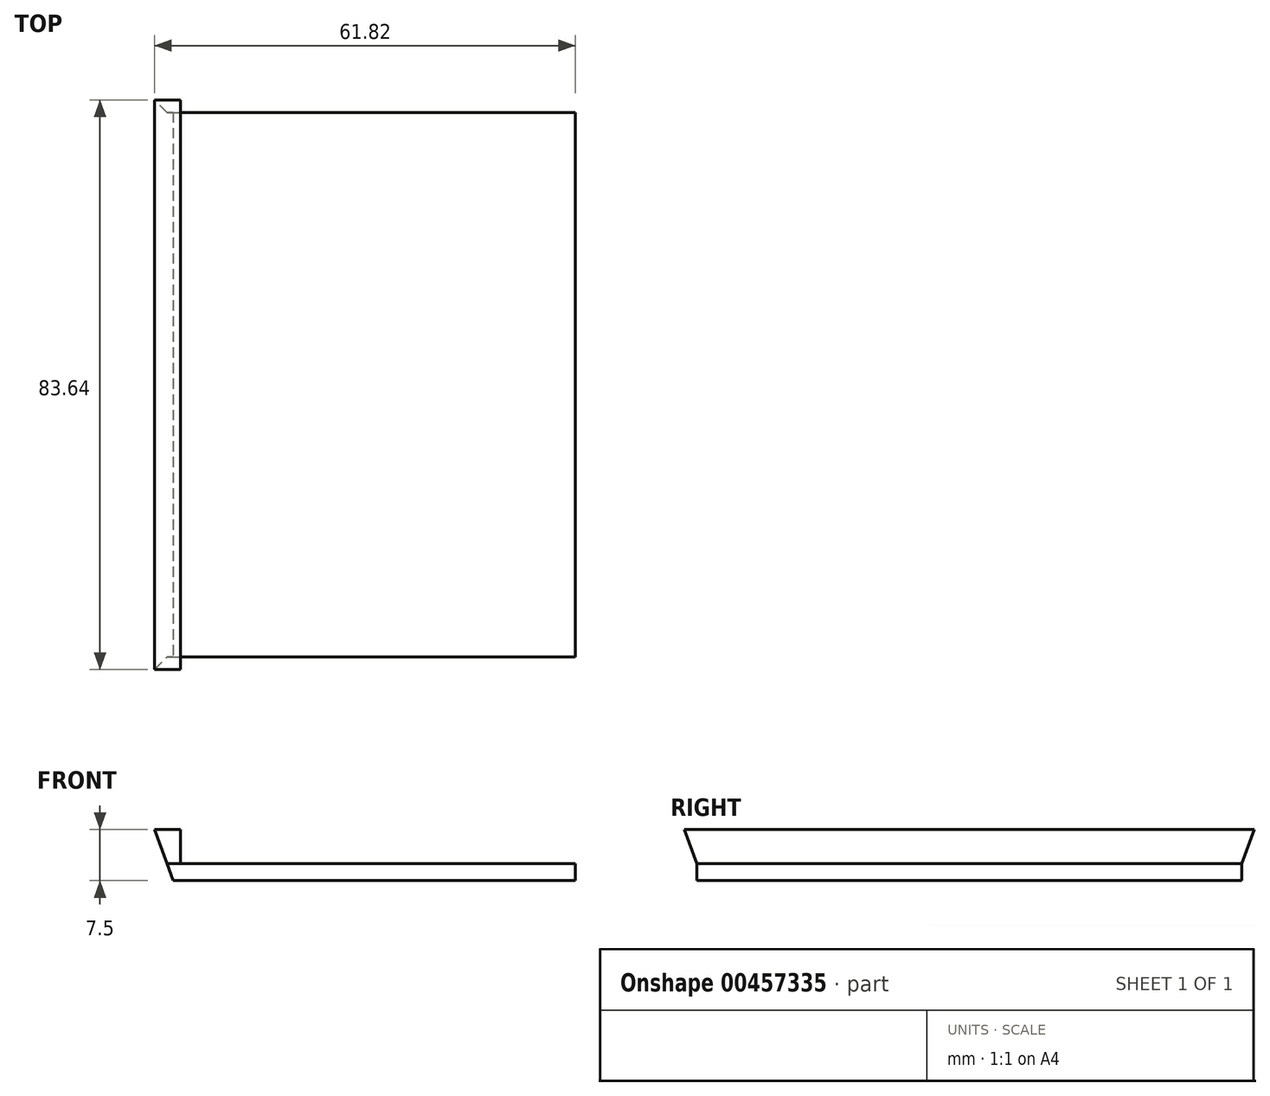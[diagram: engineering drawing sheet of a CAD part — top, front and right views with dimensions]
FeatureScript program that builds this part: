
annotation { "Feature Type Name" : "Feature", "Feature Type Description" : "" }
export const myFeature = defineFeature(function(context is Context, id is Id, definition is map)
    precondition{}
    {
        {
            var Q0;
            Q0=qCreatedBy(makeId("Top.planeOp"),FACE);
            var sketch = newSketch(context, id + "F0", { "sketchPlane" : qUnion([Q0])});
            skLineSegment(sketch, "E0.bottom", {"start": v(-22.39, 40.24) * mm, "end": v(37.61, 40.24) * mm});
            skLineSegment(sketch, "E0.top", {"start": v(-22.39, -39.76) * mm, "end": v(37.61, -39.76) * mm});
            skLineSegment(sketch, "E0.left", {"start": v(-22.39, 40.24) * mm, "end": v(-22.39, -39.76) * mm});
            skLineSegment(sketch, "E0.right", {"start": v(37.61, 40.24) * mm, "end": v(37.61, -39.76) * mm});
            skSolve(sketch);
        }
        {
            var Q0;
            Q0=makeQuery(id+"F0.imprint","IMPRINT",FACE,{"disambiguationData":[TD([[makeQuery(id+"F0.imprint","IMPRINT",EDGE,{"derivedFrom":sQuery(id+"F0.wireOp",EDGE,"E0.bottom")}),-1.0]])]});
            extrude(context, id + "F1", {"entities" : qUnion([Q0]), "depth" : 2.5 * mm});
        }
        {
            var Q0;
            Q0=makeQuery(id+"F1.opExtrude","CAP_FACE",FACE,{"disambiguationData":[OSD([sQuery(id+"F0.wireOp",EDGE,"E0.bottom"),sQuery(id+"F0.wireOp",EDGE,"E0.top"),sQuery(id+"F0.wireOp",EDGE,"E0.left"),sQuery(id+"F0.wireOp",EDGE,"E0.right")])],"isStart":false});
            var sketch = newSketch(context, id + "F2", { "sketchPlane" : qUnion([Q0])});
            skLineSegment(sketch, "E1.bottom", {"start": v(-22.39, 40.24) * mm, "end": v(-18.39, 40.24) * mm});
            skLineSegment(sketch, "E1.top", {"start": v(-22.39, -39.76) * mm, "end": v(-18.39, -39.76) * mm});
            skLineSegment(sketch, "E1.left", {"start": v(-22.39, 40.24) * mm, "end": v(-22.39, -39.76) * mm});
            skLineSegment(sketch, "E1.right", {"start": v(-18.39, 40.24) * mm, "end": v(-18.39, -39.76) * mm});
            skSolve(sketch);
        }
        {
            var Q0;
            Q0 = qSketchRegion(id + "F2", true);
            extrude(context, id + "F3", {"entities" : qUnion([Q0]), "operationType" : NewBodyOperationType.ADD, "depth" : 5 * mm, "hasDraft" : true, "draftAngle" : 20 * degree});
        }
        {
            var Q0;
            Q0=makeQuery(id+"F3.opExtrude","CAP_FACE",FACE,{"disambiguationData":[OSD([sQuery(id+"F2.wireOp",EDGE,"E1.bottom"),sQuery(id+"F2.wireOp",EDGE,"E1.top"),sQuery(id+"F2.wireOp",EDGE,"E1.left"),sQuery(id+"F2.wireOp",EDGE,"E1.right")])],"isStart":false});
            var sketch = newSketch(context, id + "F4", { "sketchPlane" : qUnion([Q0])});
            skLineSegment(sketch, "E2.bottom", {"start": v(-16.57, 42.06) * mm, "end": v(-20.39, 42.06) * mm});
            skLineSegment(sketch, "E2.top", {"start": v(-16.57, -41.58) * mm, "end": v(-20.39, -41.58) * mm});
            skLineSegment(sketch, "E2.left", {"start": v(-16.57, 42.06) * mm, "end": v(-16.57, -41.58) * mm});
            skLineSegment(sketch, "E2.right", {"start": v(-20.39, 42.06) * mm, "end": v(-20.39, -41.58) * mm});
            skSolve(sketch);
        }
        {
            var Q0;
            Q0 = qSketchRegion(id + "F4", true);
            extrude(context, id + "F5", {"entities" : qUnion([Q0]), "operationType" : NewBodyOperationType.REMOVE, "oppositeDirection" : true, "depth" : 5 * mm});
        }
        {
            var Q0;
            Q0=makeQuery(id+"F3.opExtrude","SWEPT_FACE",FACE,{"disambiguationData":[OSD([sQuery(id+"F2.wireOp",EDGE,"E1.left")])]});
            var sketch = newSketch(context, id + "F6", { "sketchPlane" : qUnion([Q0])});
            skPoint(sketch, "E3.oppositeSnap0", {"position": v(40.67, 12.67) * mm});
            skLineSegment(sketch, "E3.bottom", {"start": v(-42.06, 15.33) * mm, "end": v(40.67, 15.33) * mm});
            skLineSegment(sketch, "E3.top", {"start": v(-42.06, -13.6) * mm, "end": v(40.67, -13.6) * mm});
            skLineSegment(sketch, "E3.left", {"start": v(-42.06, 15.33) * mm, "end": v(-42.06, -13.6) * mm});
            skLineSegment(sketch, "E3.right", {"start": v(40.67, 15.33) * mm, "end": v(40.67, -13.6) * mm});
            skSolve(sketch);
        }
        {
            var Q0;
            {var subQ2=sQuery(id+"F6.wireOp",EDGE,"E3.top");Q0=makeQuery(id+"F6.imprint","IMPRINT",FACE,{"disambiguationData":[TD([[makeQuery(id+"F6.imprint","IMPRINT",EDGE,{"derivedFrom":subQ2}),1.0]])]});}
            extrude(context, id + "F7", {"entities" : qUnion([Q0]), "operationType" : NewBodyOperationType.REMOVE, "depth" : 25 * mm});
        }
    });
